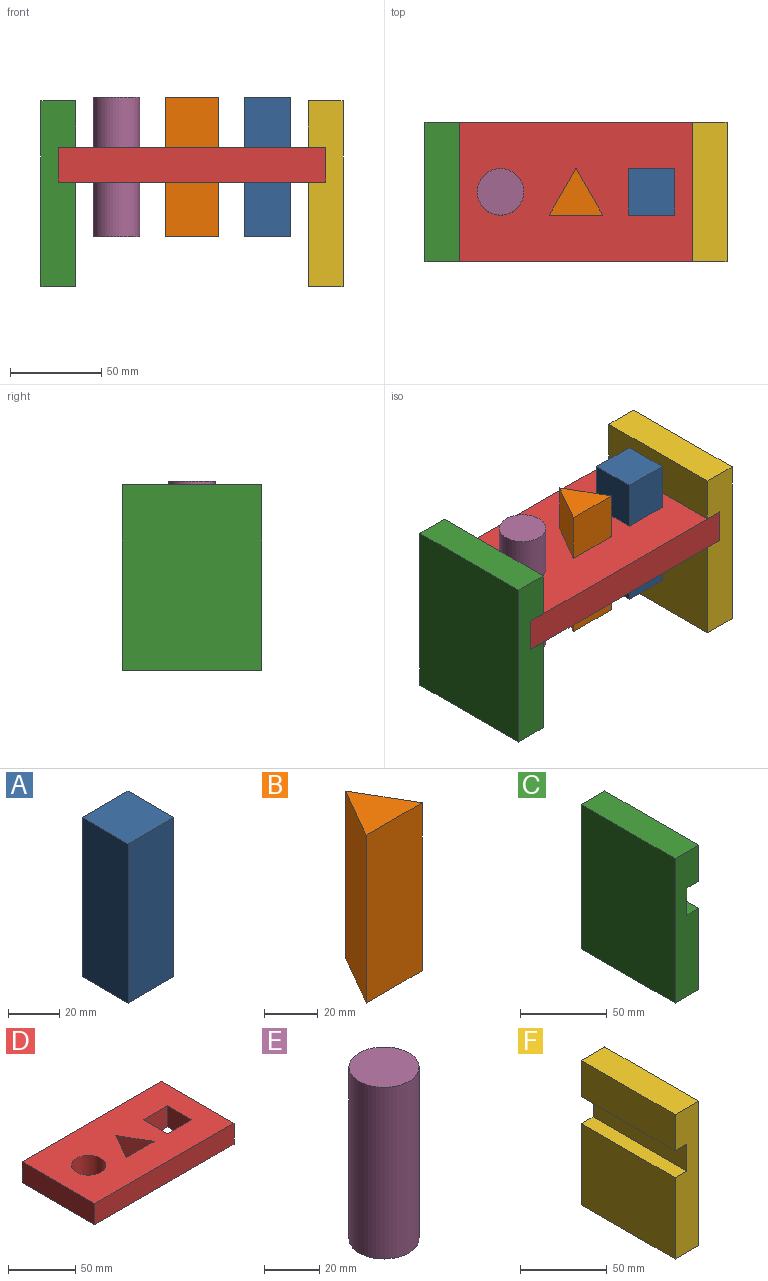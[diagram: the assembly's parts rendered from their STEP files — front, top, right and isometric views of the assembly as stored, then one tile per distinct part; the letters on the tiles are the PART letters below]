
ASSEMBLY  parts=6 mates=6
PART A: 6 faces, bbox 25.4x25.4x76.2 mm
  f0: plane 76.2x25.4mm, normal (0,1,0), area 1935.5mm2, adj f1,f3,f4,f5
  f1: plane 76.2x25.4mm, normal (-1,0,0), area 1935.5mm2, adj f0,f2,f4,f5
  f2: plane 76.2x25.4mm, normal (0,-1,0), area 1935.5mm2, adj f1,f3,f4,f5
  f3: plane 76.2x25.4mm, normal (1,0,0), area 1935.5mm2, adj f0,f2,f4,f5
  f4: plane 25.4x25.4mm, normal (0,0,1), area 645.2mm2, adj f0,f1,f2,f3
  f5: plane 25.4x25.4mm, normal (0,0,-1), area 645.2mm2, adj f0,f1,f2,f3
PART B: 5 faces, bbox 29.3x25.4x76.2 mm
  f0: plane 76.2x25.4mm, normal (-0.87,0.5,0), area 2234.9mm2, adj f1,f2,f3,f4
  f1: plane 76.2x29.33mm, normal (0,-1,0), area 2234.9mm2, adj f0,f2,f3,f4
  f2: plane 76.2x25.4mm, normal (0.87,0.5,0), area 2234.9mm2, adj f0,f1,f3,f4
  f3: plane 29.33x25.4mm, normal (0,0,1), area 372.5mm2, adj f0,f1,f2
  f4: plane 29.33x25.4mm, normal (0,0,-1), area 372.5mm2, adj f0,f1,f2
PART C: 10 faces, bbox 19.1x76.2x101.6 mm
  f0: plane 76.2x57.15mm, normal (1,0,0), area 4354.8mm2, adj f1,f7,f8,f9
  f1: plane 76.2x9.53mm, normal (0,0,1), area 725.8mm2, adj f0,f2,f8,f9
  f2: plane 76.2x19.05mm, normal (1,0,0), area 1451.6mm2, adj f1,f3,f8,f9
  f3: plane 76.2x9.53mm, normal (0,0,-1), area 725.8mm2, adj f2,f4,f8,f9
  f4: plane 76.2x25.4mm, normal (1,0,0), area 1935.5mm2, adj f3,f5,f8,f9
  f5: plane 76.2x19.05mm, normal (0,0,1), area 1451.6mm2, adj f4,f6,f8,f9
  f6: plane 101.6x76.2mm, normal (-1,0,0), area 7741.9mm2, adj f5,f7,f8,f9
  f7: plane 76.2x19.05mm, normal (0,0,-1), area 1451.6mm2, adj f0,f6,f8,f9
  f8: plane 101.6x19.05mm, normal (0,-1,0), area 1754mm2, adj f0,f1,f2,f3,f4,f5,f6,f7
  f9: plane 101.6x19.05mm, normal (0,1,0), area 1754mm2, adj f0,f1,f2,f3,f4,f5,f6,f7
PART D: 14 faces, bbox 146.1x76.2x19.1 mm
  f0: plane 146.05x76.2mm, normal (0,0,1), area 9604.7mm2, adj f2,f3,f4,f5,f6,f7,f8,f9
  f1: plane 146.05x76.2mm, normal (0,0,-1), area 9604.7mm2, adj f2,f3,f4,f5,f6,f7,f8,f9
  f2: plane 146.05x19.05mm, normal (0,1,0), area 2782.3mm2, adj f0,f1,f3,f5
  f3: plane 76.2x19.05mm, normal (-1,0,0), area 1451.6mm2, adj f0,f1,f2,f4
  f4: plane 146.05x19.05mm, normal (0,-1,0), area 2782.3mm2, adj f0,f1,f3,f5
  f5: plane 76.2x19.05mm, normal (1,0,0), area 1451.6mm2, adj f0,f1,f2,f4
  f6: plane 25.4x19.05mm, normal (0,-1,0), area 483.9mm2, adj f0,f1,f7,f9
  f7: plane 25.4x19.05mm, normal (1,0,0), area 483.9mm2, adj f0,f1,f6,f8
  f8: plane 25.4x19.05mm, normal (0,1,0), area 483.9mm2, adj f0,f1,f7,f9
  f9: plane 25.4x19.05mm, normal (-1,0,0), area 483.9mm2, adj f0,f1,f6,f8
  f10: cylinder r=12.7mm len=25.4mm, axis (0,0,1), area 1520.1mm2, adj f0,f1
  f11: plane 25.4x19.05mm, normal (0.87,-0.5,0), area 558.7mm2, adj f0,f1,f12,f13
  f12: plane 29.33x19.05mm, normal (0,1,0), area 558.7mm2, adj f0,f1,f11,f13
  f13: plane 25.4x19.05mm, normal (-0.87,-0.5,0), area 558.7mm2, adj f0,f1,f11,f12
PART E: 3 faces, bbox 25.4x25.4x76.2 mm
  f0: cylinder r=12.7mm len=76.2mm, axis (0,0,-1), area 6080.5mm2, adj f1,f2
  f1: plane 25.4x25.4mm, normal (0,0,1), area 506.7mm2, adj f0
  f2: plane 25.4x25.4mm, normal (0,0,-1), area 506.7mm2, adj f0
PART F: 10 faces, bbox 19.1x76.2x101.6 mm
  f0: plane 76.2x9.53mm, normal (0,0,1), area 725.8mm2, adj f1,f7,f8,f9
  f1: plane 76.2x57.15mm, normal (-1,0,0), area 4354.8mm2, adj f0,f2,f8,f9
  f2: plane 76.2x19.05mm, normal (0,0,-1), area 1451.6mm2, adj f1,f3,f8,f9
  f3: plane 101.6x76.2mm, normal (1,0,0), area 7741.9mm2, adj f2,f4,f8,f9
  f4: plane 76.2x19.05mm, normal (0,0,1), area 1451.6mm2, adj f3,f5,f8,f9
  f5: plane 76.2x25.4mm, normal (-1,0,0), area 1935.5mm2, adj f4,f6,f8,f9
  f6: plane 76.2x9.53mm, normal (0,0,-1), area 725.8mm2, adj f5,f7,f8,f9
  f7: plane 76.2x19.05mm, normal (-1,0,0), area 1451.6mm2, adj f0,f6,f8,f9
  f8: plane 101.6x19.05mm, normal (0,-1,0), area 1754mm2, adj f0,f1,f2,f3,f4,f5,f6,f7
  f9: plane 101.6x19.05mm, normal (0,1,0), area 1754mm2, adj f0,f1,f2,f3,f4,f5,f6,f7
PLACE A t=(29.69,45.23,-79.87)mm
PLACE B t=(29.48,-3.15,-79.87)mm
PLACE C t=(-53.33,78.33,-64.74)mm
PLACE D t=(22.55,42.57,-49.95)mm
PLACE E t=(-47,40.23,-79.87)mm
PLACE F t=(39.89,78.33,-77.62)mm
MATE slider D.f0 <-> A.f4  axis (0,0,1) through (35.55,40.23,-30.9)mm
MATE slider E.f0 <-> D.f10  axis (0,0,1) through (-47,40.23,-3.67)mm
MATE slider B.f3 <-> D.f0  axis (0,0,1) through (-5.72,36,-3.67)mm
MATE fastened F.f7 <-> D.f5  axis (-1,0,0) through (67.3,40.23,-40.43)mm
MATE fastened C.f2 <-> D.f3  axis (1,0,0) through (-78.75,40.23,-40.43)mm
MATE slider E.f0 <-> D.f10  axis (0,0,-1) through (-47,40.23,-3.67)mm
